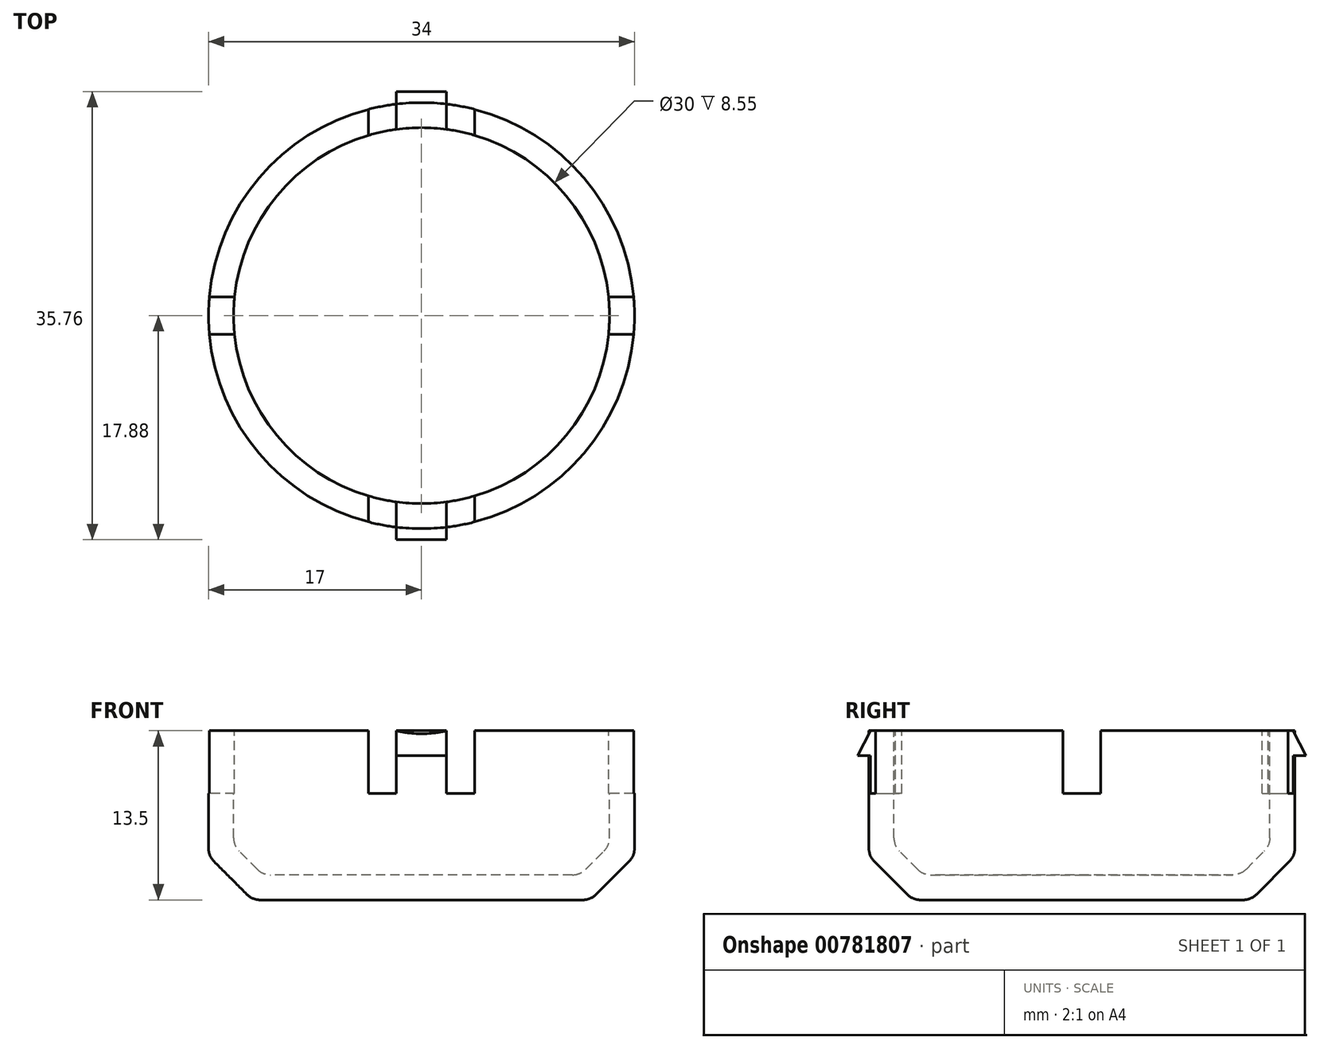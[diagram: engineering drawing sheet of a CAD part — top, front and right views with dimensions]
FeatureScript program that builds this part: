
annotation { "Feature Type Name" : "Feature", "Feature Type Description" : "" }
export const myFeature = defineFeature(function(context is Context, id is Id, definition is map)
    precondition{}
    {
        {
            var Q0;
            Q0=qCreatedBy(makeId("Front.planeOp"),FACE);
            var sketch = newSketch(context, id + "F0", { "sketchPlane" : qUnion([Q0])});
            skLineSegment(sketch, "E0", {"start": v(0, 0) * mm, "end": v(13.5, 0) * mm});
            skLineSegment(sketch, "E1", {"start": v(13.5, 0) * mm, "end": v(17, 3.5) * mm});
            skLineSegment(sketch, "E2", {"start": v(17, 3.5) * mm, "end": v(17, 13.5) * mm});
            skLineSegment(sketch, "E3.0", {"start": v(15, 4.33) * mm, "end": v(15, 13.5) * mm});
            skLineSegment(sketch, "E3.1", {"start": v(12.67, 2) * mm, "end": v(15, 4.33) * mm});
            skLineSegment(sketch, "E3.2", {"start": v(0, 2) * mm, "end": v(12.67, 2) * mm});
            skLineSegment(sketch, "E4", {"start": v(0, 2) * mm, "end": v(0, 0) * mm});
            skLineSegment(sketch, "E5", {"start": v(15, 13.5) * mm, "end": v(17, 13.5) * mm});
            skSolve(sketch);
        }
        {
            var Q0;
            Q0=makeQuery(id+"F0.imprint","IMPRINT",FACE,{"disambiguationData":[TD([[makeQuery(id+"F0.imprint","IMPRINT",EDGE,{"derivedFrom":sQuery(id+"F0.wireOp",EDGE,"E0")}),1.0]])]});
            var Q1;
            Q1=sQuery(id+"F0.wireOp",EDGE,"E4");
            revolve(context, id + "F1", {"surfaceOperationType" : NewSurfaceOperationType.NEW, "entities" : qUnion([Q0]), "axis" : qUnion([Q1]), "revolveType" : RevolveType.FULL});
        }
        {
            var Q0;
            Q0=qCreatedBy(makeId("Right.planeOp"),FACE);
            var sketch = newSketch(context, id + "F2", { "sketchPlane" : qUnion([Q0])});
            skLineSegment(sketch, "E6.bottom", {"start": v(1.5, 15) * mm, "end": v(-1.5, 15) * mm});
            skLineSegment(sketch, "E6.top", {"start": v(1.5, 8.5) * mm, "end": v(-1.5, 8.5) * mm});
            skLineSegment(sketch, "E6.left", {"start": v(1.5, 15) * mm, "end": v(1.5, 8.5) * mm});
            skLineSegment(sketch, "E6.right", {"start": v(-1.5, 15) * mm, "end": v(-1.5, 8.5) * mm});
            skPoint(sketch, "E6.middle", {"position": v(0, 11.75) * mm});
            skSolve(sketch);
        }
        {
            var Q0;
            Q0=makeQuery(id+"F2.imprint","IMPRINT",FACE,{"disambiguationData":[TD([[makeQuery(id+"F2.imprint","IMPRINT",EDGE,{"derivedFrom":sQuery(id+"F2.wireOp",EDGE,"E6.bottom")}),1.0]])]});
            extrude(context, id + "F3", {"entities" : qUnion([Q0]), "operationType" : NewBodyOperationType.REMOVE, "depth" : 25 * mm, "offsetDistance" : 25 * mm, "hasSecondDirection" : true, "secondDirectionOppositeDirection" : true, "secondDirectionDepth" : 25 * mm});
        }
        {
            var Q0;
            Q0=qCreatedBy(makeId("Front.planeOp"),FACE);
            var sketch = newSketch(context, id + "F4", { "sketchPlane" : qUnion([Q0])});
            skLineSegment(sketch, "E7.bottom", {"start": v(4.25, 15) * mm, "end": v(-4.25, 15) * mm});
            skLineSegment(sketch, "E7.top", {"start": v(4.25, 8.5) * mm, "end": v(-4.25, 8.5) * mm});
            skLineSegment(sketch, "E7.left", {"start": v(4.25, 15) * mm, "end": v(4.25, 8.5) * mm});
            skLineSegment(sketch, "E7.right", {"start": v(-4.25, 15) * mm, "end": v(-4.25, 8.5) * mm});
            skPoint(sketch, "E7.middle", {"position": v(0, 11.75) * mm});
            skLineSegment(sketch, "E8.bottom", {"start": v(2, 15) * mm, "end": v(-2, 15) * mm});
            skLineSegment(sketch, "E8.top", {"start": v(2, 8.5) * mm, "end": v(-2, 8.5) * mm});
            skLineSegment(sketch, "E8.left", {"start": v(2, 15) * mm, "end": v(2, 8.5) * mm});
            skLineSegment(sketch, "E8.right", {"start": v(-2, 15) * mm, "end": v(-2, 8.5) * mm});
            skSolve(sketch);
        }
        {
            var Q0;
            {var subQ0=sQuery(id+"F4.wireOp",EDGE,"E7.right");Q0=makeQuery(id+"F4.imprint","IMPRINT",FACE,{"disambiguationData":[TD([[makeQuery(id+"F4.imprint","IMPRINT",EDGE,{"derivedFrom":subQ0}),1.0]])]});}
            var Q1;
            {var subQ0=sQuery(id+"F4.wireOp",EDGE,"E7.left");Q1=makeQuery(id+"F4.imprint","IMPRINT",FACE,{"disambiguationData":[TD([[makeQuery(id+"F4.imprint","IMPRINT",EDGE,{"derivedFrom":subQ0}),-1.0]])]});}
            extrude(context, id + "F5", {"entities" : qUnion([Q0, Q1]), "operationType" : NewBodyOperationType.REMOVE, "depth" : 25 * mm, "offsetDistance" : 25 * mm, "hasSecondDirection" : true, "secondDirectionOppositeDirection" : true, "secondDirectionDepth" : 25 * mm});
        }
        {
            var Q0;
            Q0=makeQuery(id+"F1.opRevolve","SWEPT_EDGE",EDGE,{"disambiguationData":[OSD([sQuery(id+"F0.wireOp",EDGE,"E3.1"),sQuery(id+"F0.wireOp",EDGE,"E3.2")])]});
            var Q1;
            Q1=makeQuery(id+"F1.opRevolve","SWEPT_EDGE",EDGE,{"disambiguationData":[OSD([sQuery(id+"F0.wireOp",EDGE,"E3.0"),sQuery(id+"F0.wireOp",EDGE,"E3.1")])]});
            var Q2;
            Q2=makeQuery(id+"F1.opRevolve","SWEPT_EDGE",EDGE,{"disambiguationData":[OSD([sQuery(id+"F0.wireOp",EDGE,"E1"),sQuery(id+"F0.wireOp",EDGE,"E2")])]});
            var Q3;
            Q3=makeQuery(id+"F1.opRevolve","SWEPT_EDGE",EDGE,{"disambiguationData":[OSD([sQuery(id+"F0.wireOp",EDGE,"E0"),sQuery(id+"F0.wireOp",EDGE,"E1")])]});
            fillet(context, id + "F6", {"entities" : qUnion([Q0, Q1, Q2, Q3]), "radius" : 1.5 * mm, "tangentPropagation" : true, "allowEdgeOverflow" : false});
        }
        {
            var Q0;
            Q0=qCreatedBy(makeId("Front.planeOp"),FACE);
            cPlane(context, id + "F7", {"entities" : qUnion([Q0]), "cplaneType" : CPlaneType.OFFSET, "offset" : 16.88 * mm, "width" : 150 * mm, "height" : 150 * mm});
        }
        {
            var Q0;
            Q0=qCreatedBy(id+"F7.planeOp",FACE);
            var sketch = newSketch(context, id + "F8", { "sketchPlane" : qUnion([Q0])});
            skLineSegment(sketch, "E9.bottom", {"start": v(-2, 13.5) * mm, "end": v(2, 13.5) * mm});
            skLineSegment(sketch, "E9.top", {"start": v(-2, 11.5) * mm, "end": v(2, 11.5) * mm});
            skLineSegment(sketch, "E9.left", {"start": v(-2, 13.5) * mm, "end": v(-2, 11.5) * mm});
            skLineSegment(sketch, "E9.right", {"start": v(2, 13.5) * mm, "end": v(2, 11.5) * mm});
            skPoint(sketch, "E9.middle", {"position": v(0, 12.5) * mm});
            skSolve(sketch);
        }
        {
            var Q0;
            Q0=makeQuery(id+"F8.imprint","IMPRINT",FACE,{"disambiguationData":[TD([[makeQuery(id+"F8.imprint","IMPRINT",EDGE,{"derivedFrom":sQuery(id+"F8.wireOp",EDGE,"E9.bottom")}),-1.0]])]});
            extrude(context, id + "F9", {"entities" : qUnion([Q0]), "depth" : 1 * mm, "offsetDistance" : 25 * mm});
        }
        {
            var Q0;
            Q0=makeQuery(id+"F9.opExtrude","CAP_EDGE",EDGE,{"disambiguationData":[OSD([sQuery(id+"F8.wireOp",EDGE,"E9.bottom")])],"isStart":false});
            chamfer(context, id + "F10", {"entities" : qUnion([Q0]), "chamferType" : ChamferType.TWO_OFFSETS, "width1" : 1 * mm, "oppositeDirection" : false, "width2" : 2 * mm, "tangentPropagation" : true});
        }
        {
            var Q0;
            Q0=makeQuery(id+"F9.opExtrude","SWEPT_BODY",BODY,{"disambiguationData":[OSD([sQuery(id+"F8.wireOp",EDGE,"E9.bottom"),sQuery(id+"F8.wireOp",EDGE,"E9.top"),sQuery(id+"F8.wireOp",EDGE,"E9.left"),sQuery(id+"F8.wireOp",EDGE,"E9.right")])]});
            var Q1;
            Q1=qCreatedBy(makeId("Front.planeOp"),FACE);
            mirror(context, id + "F11", {"operationType" : NewBodyOperationType.ADD, "entities" : qUnion([Q0]), "mirrorPlane" : qUnion([Q1])});
        }
    });
